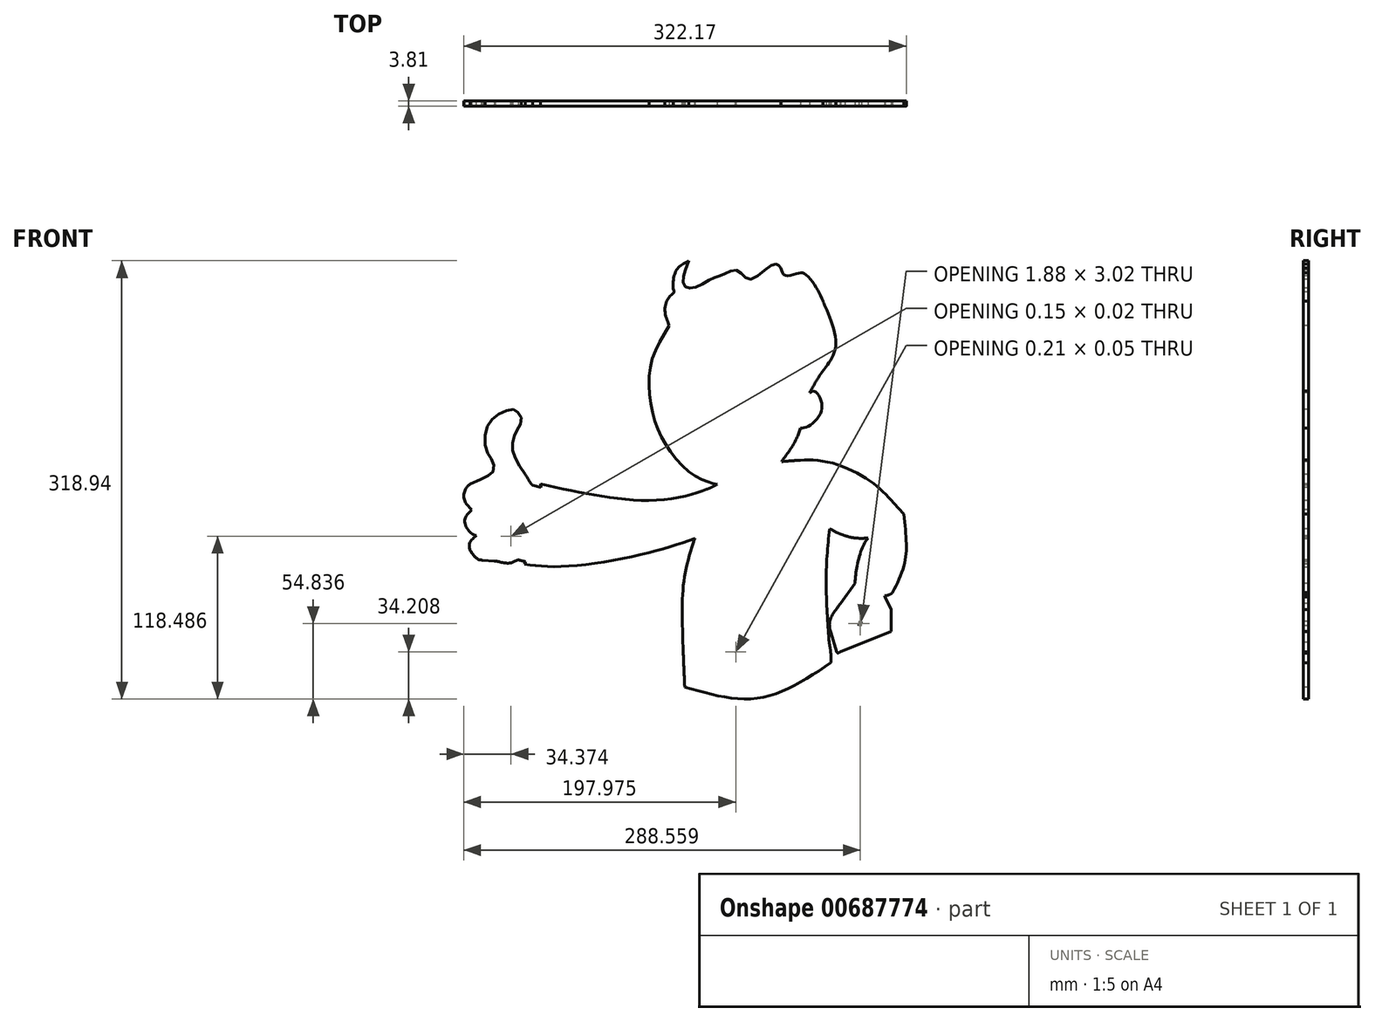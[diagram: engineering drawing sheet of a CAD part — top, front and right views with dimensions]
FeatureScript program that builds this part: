
annotation { "Feature Type Name" : "Feature", "Feature Type Description" : "" }
export const myFeature = defineFeature(function(context is Context, id is Id, definition is map)
    precondition{}
    {
        {
            var Q0;
            Q0=qCreatedBy(makeId("Front.planeOp"),FACE);
            var sketch = newSketch(context, id + "F0", { "sketchPlane" : qUnion([Q0])});
            skFitSpline(sketch, "E0", {"points": [v(50.13, 110.54) * mm, v(59.42, 125.93) * mm, v(69.05, 147.45) * mm, v(59.82, 176.78) * mm, v(59.82, 177.15) * mm], "startDerivative": vector(29.75, 55.27) * mm, "endDerivative": vector(2.31, 5.04) * mm});
            skFitSpline(sketch, "E1", {"points": [v(-32.08, 166.14) * mm, v(-26.7, 166.14) * mm, v(-15.06, 171.52) * mm, v(-4.76, 175.55) * mm, v(2.41, 166.14) * mm, v(16.75, 170.18) * mm, v(24.81, 173.31) * mm, v(31.08, 166.14) * mm, v(33.77, 158.53) * mm, v(35.56, 153.6) * mm, v(48.1, 156.29) * mm, v(57.52, 154.05) * mm, v(51.25, 141.5) * mm, v(44.08, 133.89) * mm], "startDerivative": vector(88.2, -10.9) * mm, "endDerivative": vector(-84.16, -80.95) * mm});
            skFitSpline(sketch, "E2", {"points": [v(44.08, 133.89) * mm, v(54.38, 133.89) * mm, v(62.92, 130.58) * mm], "startDerivative": vector(20.66, 1.85) * mm, "endDerivative": vector(16.64, -8.92) * mm});
            skFitSpline(sketch, "E3", {"points": [v(-47.44, 143.12) * mm, v(-53.66, 138) * mm, v(-54.76, 129.95) * mm, v(-52.93, 123) * mm, v(-47.22, 118.56) * mm, v(-41.77, 124.33) * mm, v(-40.65, 130.58) * mm, v(-42.1, 138.75) * mm, v(-47.44, 143.12) * mm]});
            skFitSpline(sketch, "E4", {"points": [v(-0.6, 133.82) * mm, v(6.36, 138.75) * mm, v(18.44, 133.82) * mm, v(22.47, 129.22) * mm], "startDerivative": vector(18.6, 18.3) * mm, "endDerivative": vector(10.5, -16.47) * mm});
            skFitSpline(sketch, "E5", {"points": [v(-0.6, 133.82) * mm, v(-1.4, 132.75) * mm, v(-0.6, 131.78) * mm, v(1.27, 132.99) * mm, v(2.15, 133.82) * mm, v(3.6, 135.16) * mm, v(6.5, 136.21) * mm, v(11.42, 135.4) * mm, v(15.2, 133.82) * mm], "startDerivative": vector(-12.6, -10.27) * mm, "endDerivative": vector(21.53, -10.19) * mm});
            skFitSpline(sketch, "E6", {"points": [v(15.2, 133.82) * mm, v(16.01, 133.23) * mm, v(19.24, 130.4) * mm, v(20.69, 128.88) * mm, v(21.74, 128.4) * mm, v(22.47, 129.22) * mm], "startDerivative": vector(4.24, -2.9) * mm, "endDerivative": vector(4.07, 7.17) * mm});
            skFitSpline(sketch, "E7", {"points": [v(-21.75, 134.43) * mm, v(-25.48, 123.23) * mm, v(-35.27, 105.04) * mm, v(-35.97, 103.17) * mm, v(-35.27, 100.37) * mm, v(-32.24, 96.64) * mm, v(-31.3, 94.77) * mm], "startDerivative": vector(-10.07, -41.5) * mm, "endDerivative": vector(6.38, -17.85) * mm});
            skFitSpline(sketch, "E8", {"points": [v(-21.75, 134.43) * mm, v(-24.78, 119.73) * mm, v(-28.74, 108.77) * mm, v(-29.44, 103.4) * mm], "startDerivative": vector(-5.78, -37.33) * mm, "endDerivative": vector(-0.9, -20.57) * mm});
            skFitSpline(sketch, "E9", {"points": [v(-29.44, 103.4) * mm, v(-24.31, 96.87) * mm], "startDerivative": vector(5.13, -6.53) * mm, "endDerivative": vector(5.13, -6.53) * mm});
            skFitSpline(sketch, "E10", {"points": [v(-35.27, 82.18) * mm, v(-36.67, 76.11) * mm, v(-33.18, 65.15) * mm, v(-42.04, 73.55) * mm, v(-35.27, 82.18) * mm]});
            skLineSegment(sketch, "E11", {"start": v(-24.31, 96.87) * mm, "end": v(-31.3, 94.77) * mm});
            skFitSpline(sketch, "E12", {"points": [v(-36.33, 78.76) * mm, v(-18.4, 77.61) * mm, v(-2.48, 81.02) * mm, v(-2.48, 81.11) * mm], "startDerivative": vector(32.43, -5.7) * mm, "endDerivative": vector(-1.31, 2.33) * mm});
            skFitSpline(sketch, "E13", {"points": [v(-33.18, 66.5) * mm, v(-27.23, 65.15) * mm, v(-7.82, 65.15) * mm, v(7.83, 73.93) * mm], "startDerivative": vector(22, -6.15) * mm, "endDerivative": vector(37.03, 28.65) * mm});
            skFitSpline(sketch, "E14", {"points": [v(-2.46, 81.08) * mm, v(1.2, 82.95) * mm], "startDerivative": vector(3.67, 1.87) * mm, "endDerivative": vector(3.67, 1.87) * mm});
            skFitSpline(sketch, "E15", {"points": [v(1.2, 82.95) * mm, v(1.2, 84.33) * mm, v(2.12, 86.63) * mm, v(4.42, 86.82) * mm, v(8.56, 85.07) * mm, v(11.42, 83.87) * mm, v(13.53, 79.91) * mm, v(13.35, 75.77) * mm, v(12.52, 73.38) * mm, v(11.42, 74.67) * mm, v(11.42, 76.88) * mm, v(10.87, 79.73) * mm, v(10.04, 81.02) * mm, v(5.34, 82.3) * mm, v(1.2, 82.95) * mm]});
            skFitSpline(sketch, "E16", {"points": [v(7.83, 73.93) * mm, v(10.59, 76.88) * mm], "startDerivative": vector(2.76, 2.94) * mm, "endDerivative": vector(2.76, 2.94) * mm});
            skFitSpline(sketch, "E17", {"points": [v(60.14, 126.9) * mm, v(56.3, 128.64) * mm, v(46.2, 131) * mm, v(44.44, 130.67) * mm, v(44.1, 129.59) * mm, v(45.05, 129.31) * mm, v(48.5, 128.64) * mm, v(54.26, 127.35) * mm, v(58.83, 125.11) * mm], "startDerivative": vector(-22.37, 12.58) * mm, "endDerivative": vector(29.2, -17) * mm});
            skFitSpline(sketch, "E18", {"points": [v(57.45, 123.12) * mm, v(56.23, 124.5) * mm, v(49.05, 126.6) * mm, v(46.2, 126.94) * mm, v(45.66, 126.2) * mm, v(46.33, 125.25) * mm, v(49.11, 124.77) * mm, v(54.13, 123.62) * mm, v(56.59, 121.8) * mm], "startDerivative": vector(-7.37, 14.27) * mm, "endDerivative": vector(16.28, -15.48) * mm});
            skFitSpline(sketch, "E19", {"points": [v(45.72, 119.76) * mm, v(44.3, 120.03) * mm, v(44.44, 121.18) * mm, v(47.83, 121.18) * mm, v(50.33, 120.44) * mm, v(51.55, 119.49) * mm, v(51.82, 118.4) * mm, v(50.67, 118.13) * mm, v(49.25, 118.95) * mm, v(47.42, 119.42) * mm, v(45.72, 119.76) * mm]});
            skFitSpline(sketch, "E20", {"points": [v(42.81, 115.67) * mm, v(45.72, 115.67) * mm, v(49.45, 114) * mm], "startDerivative": vector(6.25, 0.7) * mm, "endDerivative": vector(7.01, -3.9) * mm});
            skFitSpline(sketch, "E21", {"points": [v(42.81, 115.67) * mm, v(42.2, 115.08) * mm, v(42.81, 114.88) * mm, v(43.76, 114.88) * mm, v(44.84, 114.95) * mm, v(46.06, 114.81) * mm, v(48.18, 114) * mm, v(48.97, 113.67) * mm, v(49.45, 113.74) * mm, v(49.45, 114) * mm], "startDerivative": vector(-8.93, -6.16) * mm, "endDerivative": vector(-1.3, 4.9) * mm});
            skFitSpline(sketch, "E22", {"points": [v(-15.65, 58.15) * mm, v(-11.91, 58.75) * mm, v(-6.83, 60.7) * mm, v(-5.63, 59.5) * mm, v(-5.04, 57.7) * mm, v(-7.28, 57.1) * mm, v(-11.02, 57.1) * mm, v(-15.65, 58.15) * mm]});
            skFitSpline(sketch, "E23", {"points": [v(-53.58, 144.28) * mm, v(-52.5, 144.07) * mm, v(-48.8, 146.02) * mm, v(-42.6, 149.29) * mm, v(-39.22, 150.38) * mm], "startDerivative": vector(7.02, -3.06) * mm, "endDerivative": vector(12.56, 3.33) * mm});
            skFitSpline(sketch, "E24", {"points": [v(-53.58, 144.28) * mm, v(-53.58, 145.26) * mm, v(-44.66, 150.38) * mm], "startDerivative": vector(-1.38, 3.85) * mm, "endDerivative": vector(16.14, 7.66) * mm});
            skFitSpline(sketch, "E25", {"points": [v(-44.66, 150.38) * mm, v(-39.44, 152.34) * mm, v(-37.92, 151.9) * mm, v(-37.59, 151.25) * mm, v(-39.22, 150.38) * mm], "startDerivative": vector(14.6, 6.93) * mm, "endDerivative": vector(-9.7, -3.42) * mm});
            skFitSpline(sketch, "E26", {"points": [v(8.7, 154.3) * mm, v(7.32, 153.67) * mm, v(6.69, 152.22) * mm, v(6.82, 151.03) * mm, v(7, 150.97) * mm], "startDerivative": vector(-5.03, -1.45) * mm, "endDerivative": vector(1.83, 0) * mm});
            skFitSpline(sketch, "E27", {"points": [v(7, 150.97) * mm, v(7.82, 150.46) * mm, v(10.78, 150.09) * mm, v(14.04, 148.96) * mm, v(16.94, 147.07) * mm, v(19.45, 144.74) * mm, v(20.96, 142.86) * mm, v(22.72, 143.68) * mm, v(22.15, 145.62) * mm, v(20.2, 148.64) * mm, v(17.5, 150.97) * mm, v(13.98, 153.48) * mm, v(10.27, 154.61) * mm, v(8.7, 154.3) * mm], "startDerivative": vector(14.48, -12.75) * mm, "endDerivative": vector(-23.85, -8.4) * mm});
            skFitSpline(sketch, "E28", {"points": [v(-17.29, 43.67) * mm, v(-14.75, 40.26) * mm, v(0.53, 36.43) * mm, v(24.24, 42.28) * mm, v(29.61, 55.12) * mm, v(29.61, 60.02) * mm], "startDerivative": vector(13.91, -29.26) * mm, "endDerivative": vector(-2.2, 31.94) * mm});
            skFitSpline(sketch, "E29", {"points": [v(29.61, 60.02) * mm, v(29.61, 60.9) * mm], "startDerivative": vector(0, 0.88) * mm, "endDerivative": vector(0, 0.88) * mm});
            skFitSpline(sketch, "E30", {"points": [v(-33.78, 4) * mm, v(-40.9, -22.22) * mm, v(-42.7, -53.76) * mm, v(-40.9, -103.78) * mm], "startDerivative": vector(-28.62, -88.9) * mm, "endDerivative": vector(6.18, -133.53) * mm});
            skFitSpline(sketch, "E31", {"points": [v(64.54, 11.47) * mm, v(62.05, -23.4) * mm, v(64.23, -71.35) * mm], "startDerivative": vector(-7.58, -72.7) * mm, "endDerivative": vector(6.59, -92.41) * mm});
            skFitSpline(sketch, "E32", {"points": [v(29.61, 60.31) * mm, v(37.36, 60.9) * mm, v(61.6, 60.31) * mm, v(94.7, 45.73) * mm, v(111.2, 30.12) * mm], "startDerivative": vector(44.64, 3.25) * mm, "endDerivative": vector(55.06, -61.44) * mm});
            skFitSpline(sketch, "E33", {"points": [v(75.86, 6.32) * mm, v(82.98, 4.7) * mm, v(92.43, 4.6) * mm], "startDerivative": vector(14.64, -4.26) * mm, "endDerivative": vector(18.43, 0.72) * mm});
            skFitSpline(sketch, "E34", {"points": [v(111.2, 30.12) * mm, v(118.49, 22.03) * mm], "startDerivative": vector(7.3, -8.1) * mm, "endDerivative": vector(7.3, -8.1) * mm});
            skFitSpline(sketch, "E35", {"points": [v(92.43, 4.6) * mm, v(89.16, -0.64) * mm, v(84.7, -14.75) * mm, v(82.98, -28.23) * mm], "startDerivative": vector(-13.12, -17.8) * mm, "endDerivative": vector(-2.92, -35.34) * mm});
            skFitSpline(sketch, "E36", {"points": [v(82.98, -28.23) * mm, v(72.5, -42.99) * mm], "startDerivative": vector(-10.48, -14.76) * mm, "endDerivative": vector(-10.48, -14.76) * mm});
            skFitSpline(sketch, "E37", {"points": [v(65.44, -64.38) * mm, v(69.72, -78.18) * mm], "startDerivative": vector(4.28, -13.8) * mm, "endDerivative": vector(4.28, -13.8) * mm});
            skFitSpline(sketch, "E38", {"points": [v(72.33, -78.18) * mm, v(109.5, -63.22) * mm], "startDerivative": vector(37.16, 14.96) * mm, "endDerivative": vector(37.16, 14.96) * mm});
            skFitSpline(sketch, "E39", {"points": [v(109.5, -63.22) * mm, v(109.5, -47.36) * mm], "startDerivative": vector(0, 15.86) * mm, "endDerivative": vector(0, 15.86) * mm});
            skFitSpline(sketch, "E40", {"points": [v(109.5, -47.36) * mm, v(104.96, -38.07) * mm], "startDerivative": vector(-4.53, 9.3) * mm, "endDerivative": vector(-4.53, 9.3) * mm});
            skFitSpline(sketch, "E41", {"points": [v(104.77, -41.17) * mm, v(91.36, -50.08) * mm, v(91.36, -50.53) * mm], "startDerivative": vector(-22.36, -13.52) * mm, "endDerivative": vector(1.12, -2.63) * mm});
            skFitSpline(sketch, "E42", {"points": [v(91.36, -50.08) * mm, v(85.93, -59.14) * mm], "startDerivative": vector(-5.44, -9.06) * mm, "endDerivative": vector(-5.44, -9.06) * mm});
            skFitSpline(sketch, "E43", {"points": [v(87.74, -56.12) * mm, v(85.93, -59.14) * mm, v(95, -59.14) * mm], "startDerivative": vector(-8.45, -9.38) * mm, "endDerivative": vector(20.7, 2.42) * mm});
            skFitSpline(sketch, "E44", {"points": [v(95, -58.7) * mm, v(98.62, -52.8) * mm], "startDerivative": vector(3.63, 5.9) * mm, "endDerivative": vector(3.63, 5.9) * mm});
            skFitSpline(sketch, "E45", {"points": [v(105.06, -38.26) * mm, v(104.56, -37.13) * mm], "startDerivative": vector(-0.5, 1.13) * mm, "endDerivative": vector(-0.5, 1.13) * mm});
            skFitSpline(sketch, "E46", {"points": [v(69.72, -78.18) * mm, v(70.41, -79) * mm, v(72.33, -78.18) * mm], "startDerivative": vector(1.32, -2.65) * mm, "endDerivative": vector(3.77, 2.37) * mm});
            skFitSpline(sketch, "E47", {"points": [v(110.17, -33.85) * mm, v(110.16, -33.84) * mm], "startDerivative": vector(0, 0) * mm, "endDerivative": vector(0, 0) * mm});
            skFitSpline(sketch, "E48", {"points": [v(-33.78, 4) * mm, v(-33.57, 4.26) * mm], "startDerivative": vector(0.18, 0.3) * mm, "endDerivative": vector(0.18, 0.3) * mm});
            skFitSpline(sketch, "E49", {"points": [v(-40.9, -103.78) * mm, v(13.5, -111.72) * mm, v(65.41, -86.24) * mm], "startDerivative": vector(112.06, -32.49) * mm, "endDerivative": vector(100.6, 67.15) * mm});
            skFitSpline(sketch, "E50", {"points": [v(64.23, -71.35) * mm, v(65.41, -79) * mm, v(65.41, -86.24) * mm], "startDerivative": vector(2.92, -15.13) * mm, "endDerivative": vector(-0.57, -14.64) * mm});
            skFitSpline(sketch, "E51", {"points": [v(-42.13, -75) * mm, v(-16.18, -79.13) * mm, v(27.63, -70.95) * mm, v(52.32, -59.13) * mm, v(62.83, -50.46) * mm], "startDerivative": vector(94.94, -25.3) * mm, "endDerivative": vector(54.09, 48.22) * mm});
            skFitSpline(sketch, "E52", {"points": [v(-41.47, -91.12) * mm, v(-18.12, -96.3) * mm, v(18.32, -93.46) * mm, v(50.3, -79.94) * mm, v(64.52, -72.9) * mm], "startDerivative": vector(92.5, -27.07) * mm, "endDerivative": vector(66.9, 32.65) * mm});
            skFitSpline(sketch, "E53", {"points": [v(0.53, 26.25) * mm, v(-4.3, 0.08) * mm, v(-8.09, -30.58) * mm, v(-5.36, -64.6) * mm, v(-3.68, -78.24) * mm, v(-3.89, -78.27) * mm], "startDerivative": vector(-19.33, -103.38) * mm, "endDerivative": vector(-10.4, 2.62) * mm});
            skFitSpline(sketch, "E54", {"points": [v(21.54, 27.5) * mm, v(16.27, 5.96) * mm, v(13.12, -17.56) * mm, v(11.44, -35) * mm, v(12.91, -52.84) * mm, v(16.48, -74.27) * mm], "startDerivative": vector(-28.05, -100.99) * mm, "endDerivative": vector(18.76, -106.08) * mm});
            skFitSpline(sketch, "E55", {"points": [v(43.22, 61.3) * mm, v(42.44, 49.4) * mm, v(33.94, 36.02) * mm, v(21.54, 27.5) * mm], "startDerivative": vector(2.05, -38.27) * mm, "endDerivative": vector(-37.8, -21.41) * mm});
            skFitSpline(sketch, "E56", {"points": [v(-145.77, 44.08) * mm, v(-99.83, 34.78) * mm, v(-53.62, 32.83) * mm, v(-24.87, 40.17) * mm, v(-17.29, 43.67) * mm], "startDerivative": vector(145.84, -33.23) * mm, "endDerivative": vector(48.2, 24.73) * mm});
            skFitSpline(sketch, "E57", {"points": [v(-156.74, -12.52) * mm, v(-161.16, -11.46) * mm, v(-162.17, -11.16) * mm], "startDerivative": vector(-7.13, 1.61) * mm, "endDerivative": vector(-2.2, -0.18) * mm});
            skFitSpline(sketch, "E58", {"points": [v(-145.53, 41.63) * mm, v(-151.61, 42.93) * mm], "startDerivative": vector(-5.81, 1.25) * mm, "endDerivative": vector(-5.81, 1.25) * mm});
            skFitSpline(sketch, "E59", {"points": [v(-152.1, 13.65) * mm, v(-152.56, 13.96) * mm, v(-153.22, 14.24) * mm], "startDerivative": vector(-0.82, 0.82) * mm, "endDerivative": vector(-1.34, 0.38) * mm});
            skFitSpline(sketch, "E60", {"points": [v(-153.22, 14.24) * mm, v(-152.6, 14.2) * mm, v(-151.54, 14.49) * mm], "startDerivative": vector(1.37, -0.2) * mm, "endDerivative": vector(1.96, 0.66) * mm});
            skFitSpline(sketch, "E61", {"points": [v(-189, -11.33) * mm, v(-192.36, -10.14) * mm, v(-197.81, -1.13) * mm, v(-192.6, 6.51) * mm], "startDerivative": vector(-13.42, -0.8) * mm, "endDerivative": vector(21.15, 18.09) * mm});
            skFitSpline(sketch, "E62", {"points": [v(-192.6, 6.51) * mm, v(-195.44, 7.4) * mm, v(-201.13, 16.66) * mm, v(-195.91, 25.24) * mm], "startDerivative": vector(-11.37, -0.03) * mm, "endDerivative": vector(20.78, 19.91) * mm});
            skFitSpline(sketch, "E63", {"points": [v(-151.54, 14.49) * mm, v(-150.68, 14.7) * mm, v(-148.1, 19.04) * mm, v(-147.1, 25.9) * mm, v(-147.4, 37.26) * mm, v(-147.4, 37.4) * mm], "startDerivative": vector(8.17, -0.43) * mm, "endDerivative": vector(0.09, 1.86) * mm});
            skFitSpline(sketch, "E64", {"points": [v(-147.4, 37.4) * mm, v(-147.8, 39.01) * mm, v(-149.54, 41.18) * mm, v(-151.61, 42.93) * mm], "startDerivative": vector(-0.72, 5.61) * mm, "endDerivative": vector(-5.82, 4.56) * mm});
            skFitSpline(sketch, "E65", {"points": [v(-151.61, 42.93) * mm, v(-152.66, 44.09) * mm, v(-157.02, 51) * mm], "startDerivative": vector(-2.81, 2.98) * mm, "endDerivative": vector(-7.66, 11.82) * mm});
            skFitSpline(sketch, "E66", {"points": [v(-197.17, 43.98) * mm, v(-183.66, 50.12) * mm, v(-179.9, 54.02) * mm, v(-180.97, 61.15) * mm, v(-184.47, 66.4) * mm, v(-186.22, 78.5) * mm, v(-182.45, 89.53) * mm, v(-174.51, 95.85) * mm, v(-165.9, 98.23) * mm, v(-162.03, 95.69) * mm, v(-159.84, 90.86) * mm, v(-162.3, 84.42) * mm, v(-165.04, 78.84) * mm, v(-166.36, 71.37) * mm, v(-164.2, 62.86) * mm, v(-157.02, 51) * mm], "startDerivative": vector(180.37, 86.36) * mm, "endDerivative": vector(95.72, -136.07) * mm});
            skFitSpline(sketch, "E67", {"points": [v(-195.91, 25.24) * mm, v(-170.12, 24.3) * mm], "startDerivative": vector(25.8, -0.95) * mm, "endDerivative": vector(25.8, -0.95) * mm});
            skFitSpline(sketch, "E68", {"points": [v(-166.9, 24.18) * mm, v(-161.58, 21.84) * mm, v(-160.2, 11.2) * mm, v(-164.29, 6.67) * mm, v(-192.6, 6.51) * mm], "startDerivative": vector(33.91, -4.89) * mm, "endDerivative": vector(-87.46, 5.9) * mm});
            skFitSpline(sketch, "E69", {"points": [v(-192.6, 6.51) * mm, v(-167.46, 6) * mm, v(-167.31, 6.03) * mm], "startDerivative": vector(38.67, -0.96) * mm, "endDerivative": vector(1.14, 0.36) * mm});
            skFitSpline(sketch, "E70", {"points": [v(-197.17, 43.98) * mm, v(-197.16, 43.92) * mm, v(-197.21, 43.96) * mm], "startDerivative": vector(-0.03, -0.02) * mm, "endDerivative": vector(-0.05, -0.03) * mm});
            skFitSpline(sketch, "E71", {"points": [v(-166.9, 24.18) * mm, v(-167.19, 24.16) * mm, v(-167.4, 24.24) * mm], "startDerivative": vector(-0.57, 0.07) * mm, "endDerivative": vector(-0.4, 0.06) * mm});
            skFitSpline(sketch, "E72", {"points": [v(-37.9, 206.47) * mm, v(-40.58, 199.07) * mm, v(-41.45, 188.92) * mm, v(-35.07, 186.6) * mm, v(-21.44, 193.27) * mm, v(-12.45, 196.75) * mm, v(-2.59, 199.36) * mm, v(5.83, 192.98) * mm, v(21.78, 202.84) * mm, v(27, 203.42) * mm, v(29.03, 201.1) * mm], "startDerivative": vector(-28.8, -72.3) * mm, "endDerivative": vector(29.74, -46.45) * mm});
            skFitSpline(sketch, "E73", {"points": [v(29.03, 201.1) * mm, v(32.22, 195.88) * mm, v(41.8, 197.33) * mm, v(46.14, 197.04) * mm, v(54.26, 188.05) * mm, v(59.82, 177.15) * mm], "startDerivative": vector(11.35, -40.23) * mm, "endDerivative": vector(19.55, -44.97) * mm});
            skFitSpline(sketch, "E74", {"points": [v(-189, -11.33) * mm, v(-188.14, -11.56) * mm], "startDerivative": vector(0.85, -0.29) * mm, "endDerivative": vector(0.85, -0.29) * mm});
            skFitSpline(sketch, "E75", {"points": [v(-179.52, -12.07) * mm, v(-178.5, -12.07) * mm, v(-169.81, -13.61) * mm, v(-161.93, -11.14) * mm], "startDerivative": vector(6.5, 0.95) * mm, "endDerivative": vector(24.22, 10.12) * mm});
            skFitSpline(sketch, "E76", {"points": [v(-161.93, -11.14) * mm, v(-155.9, -6.95) * mm, v(-153.19, -2.2) * mm, v(-151.97, 5.81) * mm, v(-152.1, 13.65) * mm], "startDerivative": vector(21.28, 21.91) * mm, "endDerivative": vector(-1.06, 28.7) * mm});
            skFitSpline(sketch, "E77", {"points": [v(-24.87, 40.17) * mm, v(-22.24, 35.54) * mm, v(-8.09, 27.34) * mm, v(0.53, 26.25) * mm], "startDerivative": vector(5.88, -17.7) * mm, "endDerivative": vector(24.32, 0.18) * mm});
            skFitSpline(sketch, "E78", {"points": [v(-32.08, 166.14) * mm, v(-36.7, 167.93) * mm, v(-41.64, 170.56) * mm], "startDerivative": vector(-9.85, 2.76) * mm, "endDerivative": vector(-7.14, 8.19) * mm});
            skFitSpline(sketch, "E79", {"points": [v(-48.62, 183.8) * mm, v(-52, 180.15) * mm, v(-55.34, 169.96) * mm, v(-52.23, 159.14) * mm], "startDerivative": vector(-7.04, -13.73) * mm, "endDerivative": vector(5.31, -16.1) * mm});
            skFitSpline(sketch, "E80", {"points": [v(-197.16, 43.92) * mm, v(-200.07, 40.94) * mm, v(-201.59, 33.35) * mm, v(-195.91, 25.24) * mm], "startDerivative": vector(-11.93, -9.3) * mm, "endDerivative": vector(19.13, -19.37) * mm});
            skFitSpline(sketch, "E81", {"points": [v(-197.16, 43.92) * mm, v(-175, 43.92) * mm, v(-164.96, 40.84) * mm, v(-160.78, 30.34) * mm, v(-164.73, 25.15) * mm, v(-166.9, 24.18) * mm, v(-170.12, 24.3) * mm], "startDerivative": vector(88.21, 1.7) * mm, "endDerivative": vector(-33.47, 3.56) * mm});
            skFitSpline(sketch, "E82", {"points": [v(-145.77, 44.08) * mm, v(-145.53, 41.63) * mm], "startDerivative": vector(0.23, -2.45) * mm, "endDerivative": vector(0.23, -2.45) * mm});
            skFitSpline(sketch, "E83", {"points": [v(-157.65, -14.45) * mm, v(-156.74, -12.52) * mm], "startDerivative": vector(0.92, 1.93) * mm, "endDerivative": vector(0.92, 1.93) * mm});
            skFitSpline(sketch, "E84", {"points": [v(-156.74, -12.52) * mm, v(-149.44, 0) * mm, v(-144.45, 13.1) * mm, v(-145.53, 41.63) * mm], "startDerivative": vector(25.63, 42.98) * mm, "endDerivative": vector(-8.16, 75.99) * mm});
            skFitSpline(sketch, "E85", {"points": [v(75.86, 6.32) * mm, v(71.26, 8.02) * mm, v(64.54, 11.47) * mm], "startDerivative": vector(-9.9, 3.26) * mm, "endDerivative": vector(-12.64, 6.9) * mm});
            skFitSpline(sketch, "E86", {"points": [v(64.54, 11.47) * mm, v(63.72, 12.05) * mm, v(61.99, 13.69) * mm], "startDerivative": vector(-1.93, 1.25) * mm, "endDerivative": vector(-3.09, 3.06) * mm});
            skFitSpline(sketch, "E87", {"points": [v(72.5, -42.99) * mm, v(68.2, -48.82) * mm, v(64.59, -56.32) * mm, v(65.44, -64.38) * mm], "startDerivative": vector(-13.37, -17.43) * mm, "endDerivative": vector(5.8, -24.1) * mm});
            skFitSpline(sketch, "E88", {"points": [v(104.77, -41.17) * mm, v(105.75, -40.64) * mm, v(106.47, -41.17) * mm], "startDerivative": vector(1.95, 1.54) * mm, "endDerivative": vector(1.44, -1.6) * mm});
            skFitSpline(sketch, "E89", {"points": [v(-157.65, -14.45) * mm, v(-128.26, -15.97) * mm, v(-68.84, -6.4) * mm, v(-33.57, 4.26) * mm], "startDerivative": vector(92.4, -11.33) * mm, "endDerivative": vector(100.31, 34.14) * mm});
            skFitSpline(sketch, "E90", {"points": [v(82.98, -28.23) * mm, v(85.19, -30.53) * mm, v(95.75, -34.92) * mm, v(104.56, -37.13) * mm], "startDerivative": vector(7.12, -10.3) * mm, "endDerivative": vector(22.19, -4.83) * mm});
            skFitSpline(sketch, "E91", {"points": [v(104.56, -37.13) * mm, v(106.4, -37.13) * mm, v(109.68, -35.69) * mm, v(110.45, -35.04) * mm], "startDerivative": vector(5.08, -0.79) * mm, "endDerivative": vector(2.4, 2.48) * mm});
            skFitSpline(sketch, "E92", {"points": [v(118.49, 22.03) * mm, v(120.4, 0) * mm, v(118.49, -16.17) * mm, v(110.45, -35.04) * mm], "startDerivative": vector(7.53, -64.86) * mm, "endDerivative": vector(-27.6, -56.45) * mm});
            skFitSpline(sketch, "E93", {"points": [v(43.38, 84.78) * mm, v(39.44, 74.98) * mm, v(29.61, 60.31) * mm], "startDerivative": vector(-7.22, -21.7) * mm, "endDerivative": vector(-19.79, -27.01) * mm});
            skFitSpline(sketch, "E94", {"points": [v(29.61, 60.31) * mm, v(28.9, 59.33) * mm, v(27.2, 58.02) * mm, v(27.18, 58) * mm], "startDerivative": vector(-1.06, -2.15) * mm, "endDerivative": vector(-0.08, -0.13) * mm});
            skFitSpline(sketch, "E95", {"points": [v(-17.29, 43.67) * mm, v(-23.81, 45.38) * mm, v(-37.25, 52.37) * mm, v(-53.03, 70.12) * mm, v(-62.52, 89.43) * mm, v(-66.83, 113.26) * mm, v(-64, 136.56) * mm, v(-52.23, 159.14) * mm], "startDerivative": vector(-71.14, 15.45) * mm, "endDerivative": vector(78.93, 135.15) * mm});
            skFitSpline(sketch, "E96", {"points": [v(-52.23, 159.14) * mm, v(-46.86, 166.35) * mm, v(-41.64, 170.56) * mm], "startDerivative": vector(9.66, 14.61) * mm, "endDerivative": vector(11.57, 8.08) * mm});
            skFitSpline(sketch, "E97", {"points": [v(-17.29, 43.67) * mm, v(-12.79, 43.12) * mm, v(-10.72, 43.08) * mm], "startDerivative": vector(4.13, -1.26) * mm, "endDerivative": vector(3.89, -0.12) * mm});
            skFitSpline(sketch, "E98", {"points": [v(50.13, 110.54) * mm, v(53.61, 111.45) * mm, v(58.27, 105.04) * mm, v(57.6, 94.74) * mm, v(48.8, 85.84) * mm, v(43.38, 84.78) * mm], "startDerivative": vector(24.96, 14.11) * mm, "endDerivative": vector(-29.77, -0.66) * mm});
            skFitSpline(sketch, "E99", {"points": [v(50.13, 110.54) * mm, v(48.62, 109.78) * mm, v(47.13, 108.54) * mm, v(46.8, 107.95) * mm], "startDerivative": vector(-3.96, -1.72) * mm, "endDerivative": vector(-0.97, -2.31) * mm});
            skLineSegment(sketch, "E100", {"start": v(-188.14, -11.56) * mm, "end": v(-179.52, -12.07) * mm});
            skLineSegment(sketch, "E101", {"start": v(-179.2, -12.03) * mm, "end": v(-166.1, -12.07) * mm});
            skFitSpline(sketch, "E102", {"points": [v(-167.3, 6.03) * mm, v(-162.34, 4.76) * mm, v(-160.76, -2.98) * mm, v(-162.1, -8.55) * mm, v(-166.1, -12.07) * mm], "startDerivative": vector(24.78, -0.12) * mm, "endDerivative": vector(-19.59, -13.52) * mm});
            skFitSpline(sketch, "E103", {"points": [v(-37.9, 206.47) * mm, v(-45.23, 201.8) * mm, v(-48.22, 196.8) * mm, v(-49.5, 187.52) * mm, v(-48.62, 183.8) * mm], "startDerivative": vector(-29.17, -15.9) * mm, "endDerivative": vector(6.26, -16.7) * mm});
            skFitSpline(sketch, "E104", {"points": [v(-48.62, 183.8) * mm, v(-47.15, 179.74) * mm, v(-43.2, 172.92) * mm, v(-41.64, 170.56) * mm], "startDerivative": vector(3.33, -11.6) * mm, "endDerivative": vector(5.22, -7.62) * mm});
            skSolve(sketch);
        }
        {
            var Q0;
            Q0=qSketchRegion(id+"F0",true);
            extrude(context, id + "F1", {"entities" : qUnion([Q0]), "oppositeDirection" : true, "depth" : 3.8 * mm});
        }
        {
            var Q0;
            {var subQ0=sQuery(id+"F0.wireOp",EDGE,"E10");var subQ1=makeQuery(id+"F0.imprint","IMPRINT",VERTEX,{"disambiguationData":[OD(0.0)],"derivedFrom":subQ0});Q0=makeQuery(id+"F0.imprint","IMPRINT",FACE,{"disambiguationData":[TD([[makeQuery(id+"F0.imprint","IMPRINT",EDGE,{"disambiguationData":[TD([[subQ1,-1.0]])],"derivedFrom":subQ0}),-1.0]])]});}
            var Q1;
            Q1=makeQuery(id+"F0.imprint","IMPRINT",FACE,{"disambiguationData":[TD([[makeQuery(id+"F0.imprint","IMPRINT",EDGE,{"derivedFrom":sQuery(id+"F0.wireOp",EDGE,"E22")}),-1.0]])]});
            var Q2;
            Q2=makeQuery(id+"F0.imprint","IMPRINT",FACE,{"disambiguationData":[TD([[makeQuery(id+"F0.imprint","IMPRINT",EDGE,{"derivedFrom":sQuery(id+"F0.wireOp",EDGE,"E15")}),-1.0]])]});
            var Q3;
            Q3=makeQuery(id+"F0.imprint","IMPRINT",FACE,{"disambiguationData":[TD([[makeQuery(id+"F0.imprint","IMPRINT",EDGE,{"derivedFrom":sQuery(id+"F0.wireOp",EDGE,"E7")}),1.0]])]});
            var Q4;
            Q4=makeQuery(id+"F0.imprint","IMPRINT",FACE,{"disambiguationData":[TD([[makeQuery(id+"F0.imprint","IMPRINT",EDGE,{"derivedFrom":sQuery(id+"F0.wireOp",EDGE,"E20")}),-1.0]])]});
            var Q5;
            Q5=makeQuery(id+"F0.imprint","IMPRINT",FACE,{"disambiguationData":[TD([[makeQuery(id+"F0.imprint","IMPRINT",EDGE,{"derivedFrom":sQuery(id+"F0.wireOp",EDGE,"E19")}),-1.0]])]});
            var Q6;
            Q6=makeQuery(id+"F0.imprint","IMPRINT",FACE,{"disambiguationData":[TD([[makeQuery(id+"F0.imprint","IMPRINT",EDGE,{"derivedFrom":sQuery(id+"F0.wireOp",EDGE,"E4")}),-1.0]])]});
            var Q7;
            Q7=makeQuery(id+"F0.imprint","IMPRINT",FACE,{"disambiguationData":[TD([[makeQuery(id+"F0.imprint","IMPRINT",EDGE,{"derivedFrom":sQuery(id+"F0.wireOp",EDGE,"E3")}),1.0]])]});
            var Q8;
            Q8=makeQuery(id+"F0.imprint","IMPRINT",FACE,{"disambiguationData":[TD([[makeQuery(id+"F0.imprint","IMPRINT",EDGE,{"derivedFrom":sQuery(id+"F0.wireOp",EDGE,"E26")}),1.0]])]});
            var Q9;
            Q9=makeQuery(id+"F0.imprint","IMPRINT",FACE,{"disambiguationData":[TD([[makeQuery(id+"F0.imprint","IMPRINT",EDGE,{"derivedFrom":sQuery(id+"F0.wireOp",EDGE,"E23")}),1.0]])]});
            extrude(context, id + "F2", {"entities" : qUnion([Q0, Q1, Q2, Q3, Q4, Q5, Q6, Q7, Q8, Q9]), "operationType" : NewBodyOperationType.ADD, "oppositeDirection" : true, "depth" : 3.8 * mm});
        }
    });
